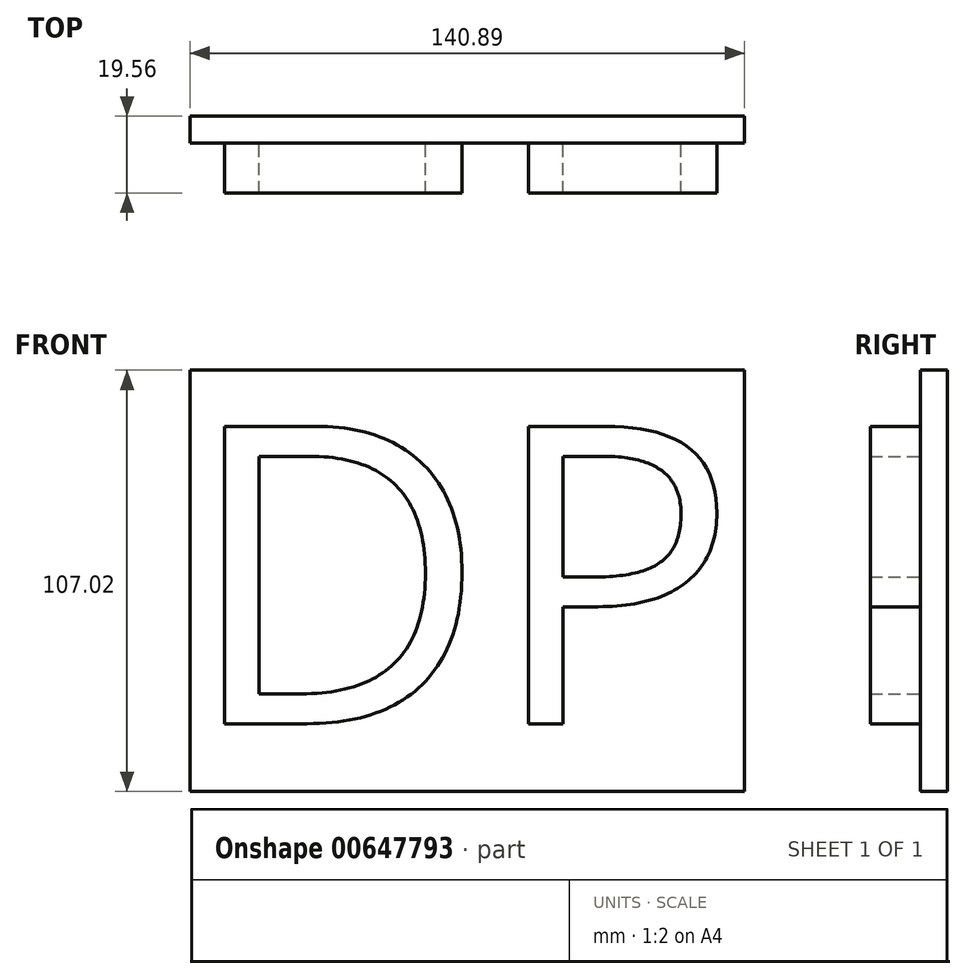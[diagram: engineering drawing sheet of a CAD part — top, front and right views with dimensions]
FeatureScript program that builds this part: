
annotation { "Feature Type Name" : "Feature", "Feature Type Description" : "" }
export const myFeature = defineFeature(function(context is Context, id is Id, definition is map)
    precondition{}
    {
        {
            var Q0;
            Q0=qCreatedBy(makeId("Front.planeOp"),FACE);
            var sketch = newSketch(context, id + "F0", { "sketchPlane" : qUnion([Q0])});
            skText(sketch, "E0", { "text": "DP", "fontName": "OpenSans-Regular.ttf"});
            const initialGuessF0  = {"E0": [-0.04762, -0.03919, 1, 0, 0.0762]};
            skSetInitialGuess(sketch, initialGuessF0);
            skSolve(sketch);
        }
        {
            var Q0;
            Q0 = qSketchRegion(id + "F0", true);
            extrude(context, id + "F1", {"entities" : qUnion([Q0]), "depth" : 12.7 * mm, "offsetDistance" : 25.4 * mm});
        }
        {
            var Q0;
            Q0=qCreatedBy(makeId("Front.planeOp"),FACE);
            var sketch = newSketch(context, id + "F2", { "sketchPlane" : qUnion([Q0])});
            skLineSegment(sketch, "E1.bottom", {"start": v(-46.03, 50.62) * mm, "end": v(94.86, 50.62) * mm});
            skLineSegment(sketch, "E1.top", {"start": v(-46.03, -56.4) * mm, "end": v(94.86, -56.4) * mm});
            skLineSegment(sketch, "E1.left", {"start": v(-46.03, 50.62) * mm, "end": v(-46.03, -56.4) * mm});
            skLineSegment(sketch, "E1.right", {"start": v(94.86, 50.62) * mm, "end": v(94.86, -56.4) * mm});
            skSolve(sketch);
        }
        {
            var Q0;
            Q0 = qSketchRegion(id + "F2", true);
            extrude(context, id + "F3", {"entities" : qUnion([Q0]), "operationType" : NewBodyOperationType.ADD, "oppositeDirection" : true, "depth" : 6.86 * mm, "offsetDistance" : 25.4 * mm});
        }
    });
